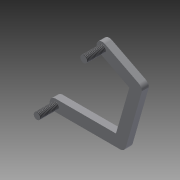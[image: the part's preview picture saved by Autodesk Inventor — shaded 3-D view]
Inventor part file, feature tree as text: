
AUTODESK INVENTOR PART (.ipt)
format: ipt  version: 2015 SP2 (Build 190223200, 223)  size: 103,936 bytes
history: native  units: mm
features: sketch x4, extrude x3, thread x2
ambient origin geometry x8: Origin, YZ Plane, XZ Plane, XY Plane, X Axis, Y Axis, Z Axis, Center Point
bodies: Solid1 (feature_tree)
feature tree (9):
  extrude  "Extrusion1"  Depth=5.0mm
  extrude  "Extrusion2"  Depth=3.0mm
  thread  "Thread3"  [1 undecoded]
  sketch  "Sketch3"  dims[d6=2.8mm d7=8.0mm d8=0.0mm d13=10.0mm d14=0.0mm]
  extrude  "Extrusion3"  Depth=8.0mm TaperAngle=0.0deg
  thread  "Thread4"  [1 undecoded]
  sketch  "Sketch1"  dims[d0=5.0mm d1=5.0mm]
  sketch  "Sketch2"  dims[d2=5.0mm d3=5.0mm d4=3.0mm d5=0.0mm]
  sketch  "Sketch4"  dims[d15=3.0mm d16=8.0mm d17=0.0mm d18=10.0mm d19=0.0mm]
note: 2 required parameter values undecoded (feature->parameter linkage not recoverable at this tier; creation-order binding heuristic only, values carry confidence <= 0.55)
